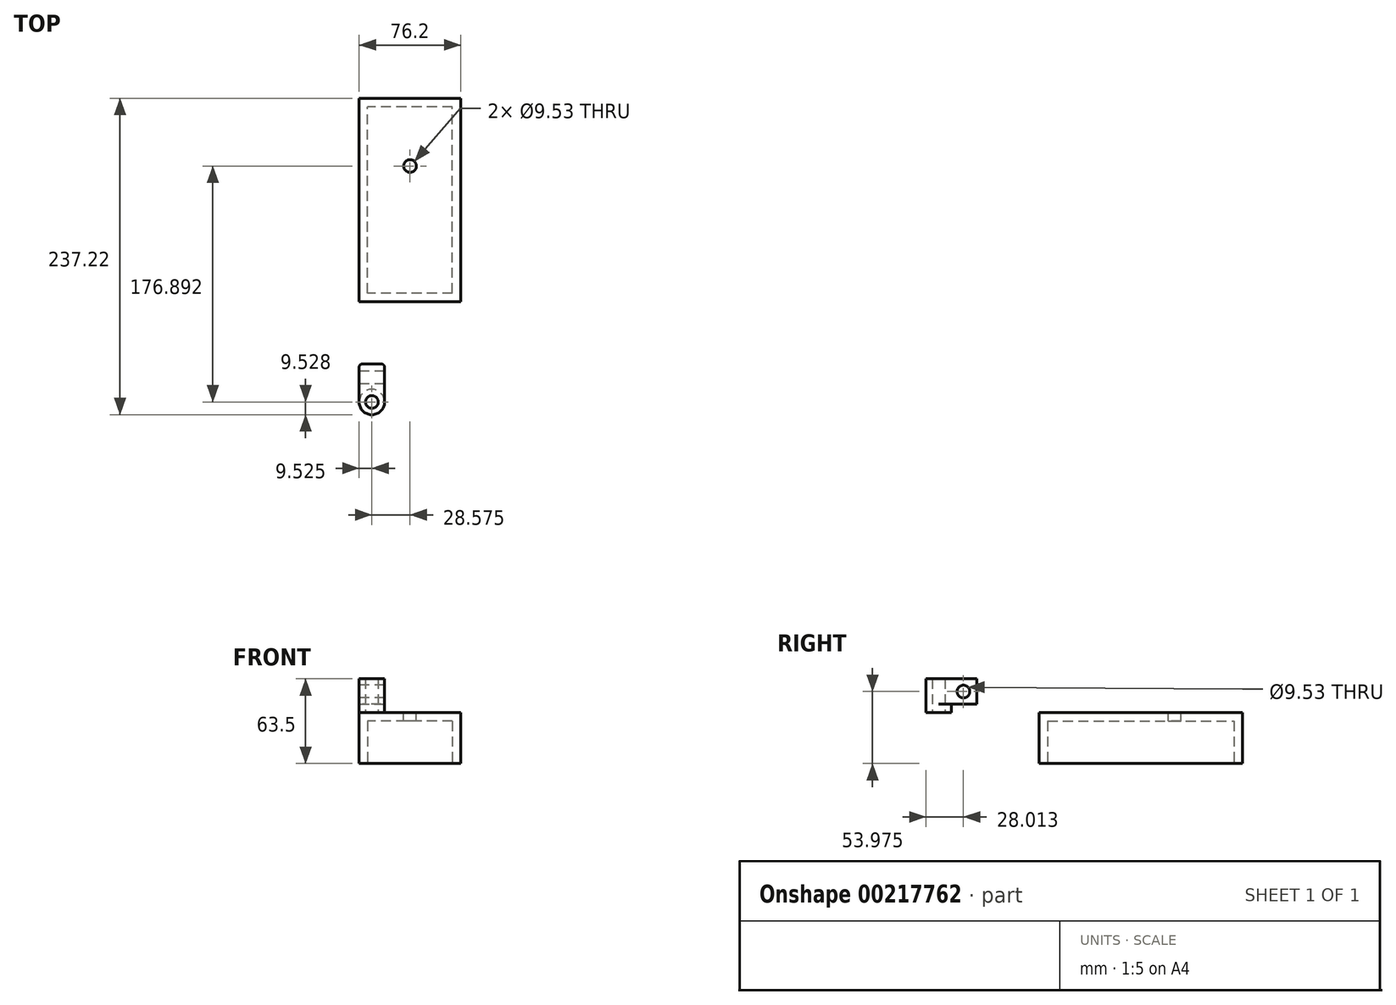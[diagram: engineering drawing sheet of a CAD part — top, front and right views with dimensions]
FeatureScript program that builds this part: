
annotation { "Feature Type Name" : "Feature", "Feature Type Description" : "" }
export const myFeature = defineFeature(function(context is Context, id is Id, definition is map)
    precondition{}
    {
        {
            var Q0;
            Q0=qCreatedBy(makeId("Top.planeOp"),FACE);
            var sketch = newSketch(context, id + "F0", { "sketchPlane" : qUnion([Q0])});
            skLineSegment(sketch, "E0.bottom", {"start": v(0, 0) * mm, "end": v(76.2, 0) * mm});
            skLineSegment(sketch, "E0.top", {"start": v(0, 152.4) * mm, "end": v(76.2, 152.4) * mm});
            skLineSegment(sketch, "E0.left", {"start": v(0, 0) * mm, "end": v(0, 152.4) * mm});
            skLineSegment(sketch, "E0.right", {"start": v(76.2, 0) * mm, "end": v(76.2, 152.4) * mm});
            skSolve(sketch);
        }
        {
            var Q0;
            Q0=makeQuery(id+"F0.imprint","IMPRINT",FACE,{"disambiguationData":[TD([[makeQuery(id+"F0.imprint","IMPRINT",EDGE,{"derivedFrom":sQuery(id+"F0.wireOp",EDGE,"E0.bottom")}),1.0]])]});
            extrude(context, id + "F1", {"entities" : qUnion([Q0]), "oppositeDirection" : true, "depth" : 38.1 * mm});
        }
        {
            var Q0;
            Q0=makeQuery(id+"F1.opExtrude","CAP_FACE",FACE,{"disambiguationData":[OSD([sQuery(id+"F0.wireOp",EDGE,"E0.bottom"),sQuery(id+"F0.wireOp",EDGE,"E0.top"),sQuery(id+"F0.wireOp",EDGE,"E0.left"),sQuery(id+"F0.wireOp",EDGE,"E0.right")])],"isStart":true});
            var sketch = newSketch(context, id + "F2", { "sketchPlane" : qUnion([Q0])});
            skCircle(sketch, "E1", {"center": v(38.1, 101.6) * mm, "radius": 4.76 * mm});
            skSolve(sketch);
        }
        {
            var Q0;
            Q0=makeQuery(id+"F1.opExtrude","CAP_FACE",FACE,{"disambiguationData":[OSD([sQuery(id+"F0.wireOp",EDGE,"E0.bottom"),sQuery(id+"F0.wireOp",EDGE,"E0.top"),sQuery(id+"F0.wireOp",EDGE,"E0.left"),sQuery(id+"F0.wireOp",EDGE,"E0.right")])],"isStart":false});
            var sketch = newSketch(context, id + "F3", { "sketchPlane" : qUnion([Q0])});
            skLineSegment(sketch, "E2.bottom", {"start": v(69.85, -6.35) * mm, "end": v(6.35, -6.35) * mm});
            skLineSegment(sketch, "E2.top", {"start": v(69.85, -146.05) * mm, "end": v(6.35, -146.05) * mm});
            skLineSegment(sketch, "E2.left", {"start": v(69.85, -6.35) * mm, "end": v(69.85, -146.05) * mm});
            skLineSegment(sketch, "E2.right", {"start": v(6.35, -6.35) * mm, "end": v(6.35, -146.05) * mm});
            skSolve(sketch);
        }
        {
            var Q0;
            Q0=makeQuery(id+"F3.imprint","IMPRINT",FACE,{"disambiguationData":[TD([[makeQuery(id+"F3.imprint","IMPRINT",EDGE,{"derivedFrom":sQuery(id+"F3.wireOp",EDGE,"E2.bottom")}),1.0]])]});
            extrude(context, id + "F4", {"entities" : qUnion([Q0]), "operationType" : NewBodyOperationType.REMOVE, "oppositeDirection" : true, "depth" : 31.75 * mm});
        }
        {
            var Q0;
            Q0=makeQuery(id+"F2.imprint","IMPRINT",FACE,{"disambiguationData":[TD([[makeQuery(id+"F2.imprint","IMPRINT",EDGE,{"derivedFrom":sQuery(id+"F2.wireOp",EDGE,"E1")}),1.0]])]});
            extrude(context, id + "F5", {"entities" : qUnion([Q0]), "operationType" : NewBodyOperationType.REMOVE, "oppositeDirection" : true, "depth" : 6.35 * mm});
        }
        {
            var Q0;
            Q0=qCreatedBy(makeId("Right.planeOp"),FACE);
            var sketch = newSketch(context, id + "F6", { "sketchPlane" : qUnion([Q0])});
            skLineSegment(sketch, "E3", {"start": v(-84.82, 0) * mm, "end": v(-84.82, 25.4) * mm});
            skLineSegment(sketch, "E4", {"start": v(-84.82, 25.4) * mm, "end": v(-46.72, 25.4) * mm});
            skLineSegment(sketch, "E5", {"start": v(-46.72, 25.4) * mm, "end": v(-46.72, 6.35) * mm});
            skLineSegment(sketch, "E6", {"start": v(-46.72, 6.35) * mm, "end": v(-65.77, 6.35) * mm});
            skLineSegment(sketch, "E7", {"start": v(-65.77, 6.35) * mm, "end": v(-65.77, 0) * mm});
            skLineSegment(sketch, "E8", {"start": v(-65.77, 0) * mm, "end": v(-84.82, 0) * mm});
            skCircle(sketch, "E9", {"center": v(-56.8, 15.88) * mm, "radius": 4.76 * mm});
            skSolve(sketch);
        }
        {
            var Q0;
            Q0=makeQuery(id+"F6.imprint","IMPRINT",FACE,{"disambiguationData":[TD([[makeQuery(id+"F6.imprint","IMPRINT",EDGE,{"derivedFrom":sQuery(id+"F6.wireOp",EDGE,"E3")}),-1.0]])]});
            extrude(context, id + "F7", {"entities" : qUnion([Q0]), "depth" : 19.05 * mm});
        }
        {
            var Q0;
            Q0=makeQuery(id+"F7.opExtrude","SWEPT_FACE",FACE,{"disambiguationData":[OSD([sQuery(id+"F6.wireOp",EDGE,"E8")])]});
            var sketch = newSketch(context, id + "F8", { "sketchPlane" : qUnion([Q0])});
            skCircle(sketch, "E10", {"center": v(9.53, 75.3) * mm, "radius": 9.53 * mm});
            skCircle(sketch, "E11", {"center": v(9.53, 75.3) * mm, "radius": 4.76 * mm});
            skLineSegment(sketch, "E12.bottom", {"start": v(19.05, 84.82) * mm, "end": v(0, 84.82) * mm});
            skLineSegment(sketch, "E12.top", {"start": v(19.05, 65.77) * mm, "end": v(0, 65.77) * mm});
            skLineSegment(sketch, "E12.left", {"start": v(19.05, 84.82) * mm, "end": v(19.05, 65.77) * mm});
            skLineSegment(sketch, "E12.right", {"start": v(0, 84.82) * mm, "end": v(0, 65.77) * mm});
            skSolve(sketch);
        }
        {
            var Q0;
            Q0=makeQuery(id+"F8.imprint","IMPRINT",FACE,{"disambiguationData":[TD([[makeQuery(id+"F8.imprint","IMPRINT",EDGE,{"derivedFrom":sQuery(id+"F8.wireOp",EDGE,"E11")}),1.0]])]});
            extrude(context, id + "F9", {"entities" : qUnion([Q0]), "operationType" : NewBodyOperationType.REMOVE, "oppositeDirection" : true, "depth" : 25.4 * mm});
        }
        {
            var Q0;
            Q0=makeQuery(id+"F7.opExtrude","SWEPT_FACE",FACE,{"disambiguationData":[OSD([sQuery(id+"F6.wireOp",EDGE,"E8")])]});
            var sketch = newSketch(context, id + "F10", { "sketchPlane" : qUnion([Q0])});
            skCircle(sketch, "E13", {"center": v(9.53, 75.3) * mm, "radius": 9.53 * mm});
            skLineSegment(sketch, "E14.bottom", {"start": v(19.05, 84.82) * mm, "end": v(0, 84.82) * mm});
            skLineSegment(sketch, "E14.top", {"start": v(19.05, 65.77) * mm, "end": v(0, 65.77) * mm});
            skLineSegment(sketch, "E14.left", {"start": v(19.05, 84.82) * mm, "end": v(19.05, 65.77) * mm});
            skLineSegment(sketch, "E14.right", {"start": v(0, 84.82) * mm, "end": v(0, 65.77) * mm});
            skSolve(sketch);
        }
        {
            var Q0;
            {var subQ0=sQuery(id+"F10.wireOp",EDGE,"E14.bottom");var subQ1=sQuery(id+"F10.wireOp",EDGE,"E13");var subQ2=makeQuery(id+"F10.imprint","INTERSECT",VERTEX,{"derivedFrom":[subQ1,subQ0]});Q0=makeQuery(id+"F10.imprint","IMPRINT",FACE,{"disambiguationData":[TD([[makeQuery(id+"F10.imprint","IMPRINT",EDGE,{"disambiguationData":[TD([[subQ2,-1.0]])],"derivedFrom":subQ1}),-1.0]])]});}
            var Q1;
            {var subQ0=sQuery(id+"F10.wireOp",EDGE,"E14.right");var subQ1=sQuery(id+"F10.wireOp",EDGE,"E13");var subQ2=makeQuery(id+"F10.imprint","INTERSECT",VERTEX,{"derivedFrom":[subQ1,subQ0]});Q1=makeQuery(id+"F10.imprint","IMPRINT",FACE,{"disambiguationData":[TD([[makeQuery(id+"F10.imprint","IMPRINT",EDGE,{"disambiguationData":[TD([[subQ2,-1.0]])],"derivedFrom":subQ1}),-1.0]])]});}
            var Q2;
            {var subQ0=sQuery(id+"F10.wireOp",EDGE,"E14.left");var subQ1=sQuery(id+"F10.wireOp",EDGE,"E13");var subQ2=makeQuery(id+"F10.imprint","INTERSECT",VERTEX,{"derivedFrom":[subQ1,subQ0]});Q2=makeQuery(id+"F10.imprint","IMPRINT",FACE,{"disambiguationData":[TD([[makeQuery(id+"F10.imprint","IMPRINT",EDGE,{"disambiguationData":[TD([[subQ2,1.0]])],"derivedFrom":subQ1}),-1.0]])]});}
            var Q3;
            Q3=makeQuery(id+"F10.imprint","IMPRINT",FACE,{"disambiguationData":[TD([[makeQuery(id+"F10.imprint","IMPRINT",EDGE,{"derivedFrom":makeQuery(id+"F9.boolean.opBoolean","COPY",EDGE,{"derivedFrom":makeQuery(id+"F9.opExtrude","CAP_EDGE",EDGE,{"disambiguationData":[OSD([sQuery(id+"F8.wireOp",EDGE,"E11")])],"isStart":true})})}),1.0]])]});
            var Q4;
            {var subQ0=sQuery(id+"F10.wireOp",EDGE,"E14.bottom");var subQ1=sQuery(id+"F10.wireOp",EDGE,"E13");var subQ2=makeQuery(id+"F10.imprint","INTERSECT",VERTEX,{"derivedFrom":[subQ1,subQ0]});Q4=makeQuery(id+"F10.imprint","IMPRINT",FACE,{"disambiguationData":[TD([[makeQuery(id+"F10.imprint","IMPRINT",EDGE,{"disambiguationData":[TD([[subQ2,1.0]])],"derivedFrom":subQ1}),-1.0]])]});}
            extrude(context, id + "F11", {"entities" : qUnion([Q0, Q1, Q2, Q3, Q4]), "operationType" : NewBodyOperationType.REMOVE, "oppositeDirection" : true, "depth" : 6.35 * mm});
        }
        {
            var Q0;
            Q0=makeQuery(id+"F7.opExtrude","SWEPT_FACE",FACE,{"disambiguationData":[OSD([sQuery(id+"F6.wireOp",EDGE,"E8")])]});
            var sketch = newSketch(context, id + "F12", { "sketchPlane" : qUnion([Q0])});
            skArc(sketch, "E15", {"start": v(19.05, 75.3) * mm, "mid": v(9.53, 84.82) * mm, "end": v(0, 75.3) * mm});
            skLineSegment(sketch, "E16", {"start": v(19.05, 75.3) * mm, "end": v(0, 75.3) * mm});
            skLineSegment(sketch, "E17.bottom", {"start": v(19.05, 75.3) * mm, "end": v(-0.93, 75.3) * mm});
            skLineSegment(sketch, "E17.top", {"start": v(19.05, 86.41) * mm, "end": v(-0.93, 86.41) * mm});
            skLineSegment(sketch, "E17.left", {"start": v(19.05, 75.3) * mm, "end": v(19.05, 86.41) * mm});
            skLineSegment(sketch, "E17.right", {"start": v(-0.93, 75.3) * mm, "end": v(-0.93, 86.41) * mm});
            skSolve(sketch);
        }
        {
            var Q0;
            {var subQ1=sQuery(id+"F12.wireOp",EDGE,"E15");Q0=makeQuery(id+"F12.imprint","IMPRINT",FACE,{"disambiguationData":[TD([[makeQuery(id+"F12.imprint","IMPRINT",EDGE,{"derivedFrom":subQ1}),-1.0]])]});}
            extrude(context, id + "F13", {"entities" : qUnion([Q0]), "operationType" : NewBodyOperationType.REMOVE, "oppositeDirection" : true, "depth" : 25.4 * mm});
        }
        {
            var Q0;
            Q0=makeQuery(id+"F7.opExtrude","CAP_EDGE",EDGE,{"disambiguationData":[OSD([sQuery(id+"F6.wireOp",EDGE,"E5")])],"isStart":false});
            var Q1;
            Q1=makeQuery(id+"F7.opExtrude","CAP_EDGE",EDGE,{"disambiguationData":[OSD([sQuery(id+"F6.wireOp",EDGE,"E5")])],"isStart":true});
            fillet(context, id + "F14", {"entities" : qUnion([Q0, Q1]), "radius" : 2.54 * mm, "tangentPropagation" : true, "allowEdgeOverflow" : false});
        }
    });
